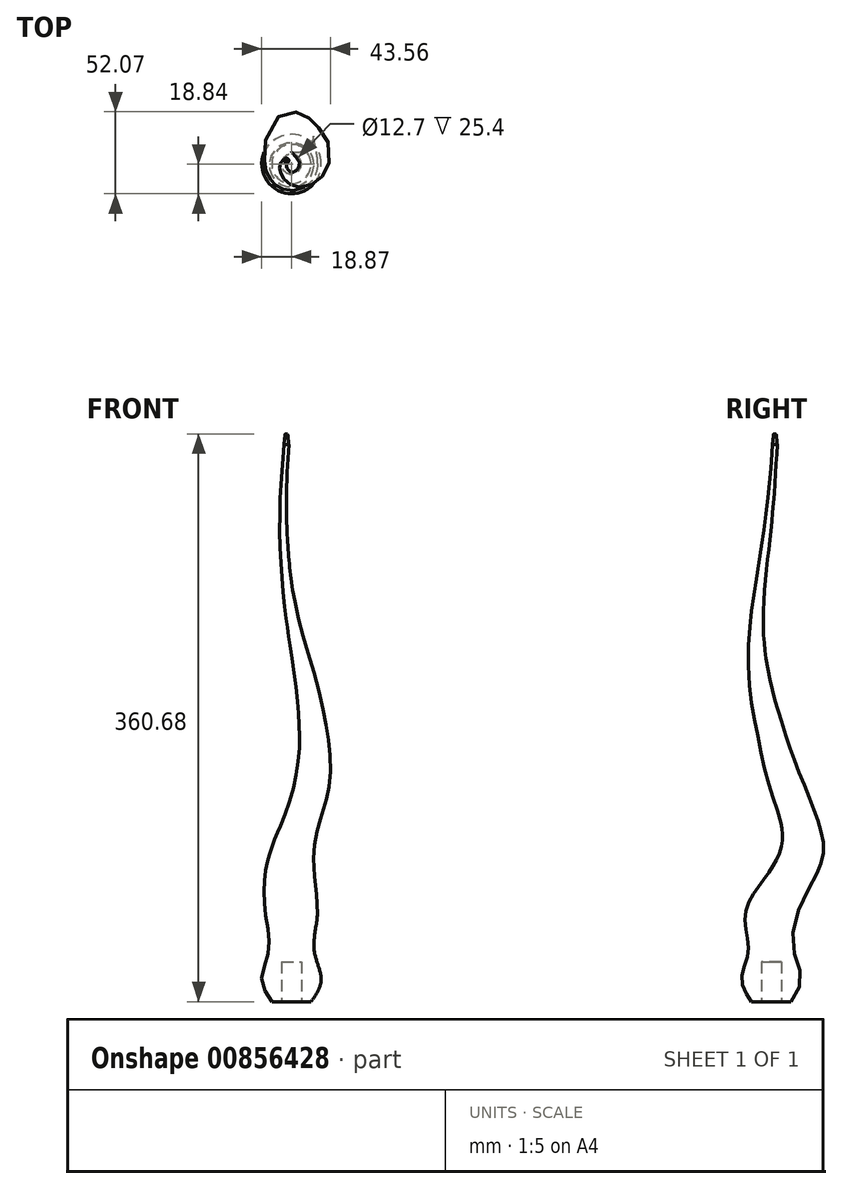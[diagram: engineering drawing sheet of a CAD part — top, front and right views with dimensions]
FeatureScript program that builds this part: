
annotation { "Feature Type Name" : "Feature", "Feature Type Description" : "" }
export const myFeature = defineFeature(function(context is Context, id is Id, definition is map)
    precondition{}
    {
        {
            var Q0;
            Q0=qCreatedBy(makeId("Top.planeOp"),FACE);
            cPlane(context, id + "F0", {"entities" : qUnion([Q0]), "cplaneType" : CPlaneType.OFFSET, "offset" : 38.1 * mm, "width" : 152.4 * mm, "height" : 152.4 * mm});
        }
        {
            var Q0;
            Q0=qCreatedBy(id+"F0.planeOp",FACE);
            cPlane(context, id + "F1", {"entities" : qUnion([Q0]), "cplaneType" : CPlaneType.OFFSET, "offset" : 38.1 * mm, "width" : 152.4 * mm, "height" : 152.4 * mm});
        }
        {
            var Q0;
            Q0=qCreatedBy(id+"F1.planeOp",FACE);
            cPlane(context, id + "F2", {"entities" : qUnion([Q0]), "cplaneType" : CPlaneType.OFFSET, "offset" : 38.1 * mm, "width" : 152.4 * mm, "height" : 152.4 * mm});
        }
        {
            var Q0;
            Q0=qCreatedBy(makeId("Top.planeOp"),FACE);
            var sketch = newSketch(context, id + "F3", { "sketchPlane" : qUnion([Q0])});
            skCircle(sketch, "E0", {"center": v(0, 0) * mm, "radius": 16.51 * mm});
            skSolve(sketch);
        }
        {
            var Q0;
            Q0=qCreatedBy(id+"F0.planeOp",FACE);
            var sketch = newSketch(context, id + "F4", { "sketchPlane" : qUnion([Q0])});
            skCircle(sketch, "E1", {"center": v(0, 19.05) * mm, "radius": 13.97 * mm});
            skLineSegment(sketch, "E2.1", {"start": v(13.47, 13.47) * mm, "end": v(19.05, 0) * mm});
            skLineSegment(sketch, "E2.2", {"start": v(19.05, 0) * mm, "end": v(13.47, -13.47) * mm});
            skLineSegment(sketch, "E2.3", {"start": v(13.47, -13.47) * mm, "end": v(0, -19.05) * mm});
            skLineSegment(sketch, "E2.4", {"start": v(0, -19.05) * mm, "end": v(-13.47, -13.47) * mm});
            skLineSegment(sketch, "E2.5", {"start": v(-13.47, -13.47) * mm, "end": v(-19.05, 0) * mm});
            skLineSegment(sketch, "E2.6", {"start": v(-19.05, 0) * mm, "end": v(-13.47, 13.47) * mm});
            skSolve(sketch);
        }
        {
            var Q0;
            Q0=qCreatedBy(id+"F1.planeOp",FACE);
            var sketch = newSketch(context, id + "F5", { "sketchPlane" : qUnion([Q0])});
            skCircle(sketch, "E3", {"center": v(11.67, 11.67) * mm, "radius": 11.43 * mm});
            skCircle(sketch, "E4.cCircle", {"center": v(0, 0) * mm, "radius": 16.51 * mm, "construction": true});
            skLineSegment(sketch, "E4.2", {"start": v(16.51, 0) * mm, "end": v(11.67, -11.67) * mm});
            skLineSegment(sketch, "E4.3", {"start": v(11.67, -11.67) * mm, "end": v(0, -16.51) * mm});
            skLineSegment(sketch, "E4.4", {"start": v(0, -16.51) * mm, "end": v(-11.67, -11.67) * mm});
            skLineSegment(sketch, "E4.5", {"start": v(-11.67, -11.67) * mm, "end": v(-16.51, 0) * mm});
            skLineSegment(sketch, "E4.6", {"start": v(-16.51, 0) * mm, "end": v(-11.67, 11.67) * mm});
            skLineSegment(sketch, "E4.7", {"start": v(-11.67, 11.67) * mm, "end": v(0, 16.51) * mm});
            skSolve(sketch);
        }
        {
            var Q0;
            Q0=qCreatedBy(id+"F2.planeOp",FACE);
            var sketch = newSketch(context, id + "F6", { "sketchPlane" : qUnion([Q0])});
            skCircle(sketch, "E5.cCircle", {"center": v(0, 0) * mm, "radius": 13.97 * mm, "construction": true});
            skLineSegment(sketch, "E5.0", {"start": v(0, -13.97) * mm, "end": v(-9.88, -9.88) * mm});
            skLineSegment(sketch, "E5.1", {"start": v(-9.88, -9.88) * mm, "end": v(-13.97, 0) * mm});
            skLineSegment(sketch, "E5.2", {"start": v(-13.97, 0) * mm, "end": v(-9.88, 9.88) * mm});
            skLineSegment(sketch, "E5.3", {"start": v(-9.88, 9.88) * mm, "end": v(0, 13.97) * mm});
            skLineSegment(sketch, "E5.4", {"start": v(0, 13.97) * mm, "end": v(9.88, 9.88) * mm});
            skLineSegment(sketch, "E5.7", {"start": v(9.88, -9.88) * mm, "end": v(0, -13.97) * mm});
            skCircle(sketch, "E6", {"center": v(13.97, 0) * mm, "radius": 8.9 * mm});
            skSolve(sketch);
        }
        {
            var Q0;
            Q0=qCreatedBy(id+"F2.planeOp",FACE);
            cPlane(context, id + "F7", {"entities" : qUnion([Q0]), "cplaneType" : CPlaneType.OFFSET, "offset" : 38.1 * mm, "width" : 152.4 * mm, "height" : 152.4 * mm});
        }
        {
            var Q0;
            Q0=qCreatedBy(id+"F7.planeOp",FACE);
            cPlane(context, id + "F8", {"entities" : qUnion([Q0]), "cplaneType" : CPlaneType.OFFSET, "offset" : 38.1 * mm, "width" : 152.4 * mm, "height" : 152.4 * mm});
        }
        {
            var Q0;
            Q0=qCreatedBy(id+"F7.planeOp",FACE);
            var sketch = newSketch(context, id + "F9", { "sketchPlane" : qUnion([Q0])});
            skCircle(sketch, "E7.cCircle", {"center": v(0, 0) * mm, "radius": 11.43 * mm, "construction": true});
            skLineSegment(sketch, "E7.0", {"start": v(0, 11.43) * mm, "end": v(8.08, 8.08) * mm});
            skLineSegment(sketch, "E7.1", {"start": v(8.08, 8.08) * mm, "end": v(11.43, 0) * mm});
            skLineSegment(sketch, "E7.4", {"start": v(0, -11.43) * mm, "end": v(-8.08, -8.08) * mm});
            skLineSegment(sketch, "E7.5", {"start": v(-8.08, -8.08) * mm, "end": v(-11.43, 0) * mm});
            skLineSegment(sketch, "E7.6", {"start": v(-11.43, 0) * mm, "end": v(-8.08, 8.08) * mm});
            skLineSegment(sketch, "E7.7", {"start": v(-8.08, 8.08) * mm, "end": v(0, 11.43) * mm});
            skCircle(sketch, "E8", {"center": v(8.08, -8.08) * mm, "radius": 6.35 * mm});
            skSolve(sketch);
        }
        {
            var Q0;
            Q0=qCreatedBy(id+"F8.planeOp",FACE);
            var sketch = newSketch(context, id + "F10", { "sketchPlane" : qUnion([Q0])});
            skCircle(sketch, "E9.cCircle", {"center": v(0, 0) * mm, "radius": 8.9 * mm, "construction": true});
            skLineSegment(sketch, "E9.0", {"start": v(0, 8.9) * mm, "end": v(6.29, 6.29) * mm});
            skLineSegment(sketch, "E9.1", {"start": v(6.29, 6.29) * mm, "end": v(8.9, 0) * mm});
            skLineSegment(sketch, "E9.2", {"start": v(8.9, 0) * mm, "end": v(6.29, -6.29) * mm});
            skLineSegment(sketch, "E9.5", {"start": v(-6.29, -6.29) * mm, "end": v(-8.9, 0) * mm});
            skLineSegment(sketch, "E9.6", {"start": v(-8.9, 0) * mm, "end": v(-6.29, 6.29) * mm});
            skLineSegment(sketch, "E9.7", {"start": v(-6.29, 6.29) * mm, "end": v(0, 8.9) * mm});
            skCircle(sketch, "E10", {"center": v(0, -8.9) * mm, "radius": 3.8 * mm});
            skSolve(sketch);
        }
        {
            var Q0;
            Q0=qCreatedBy(id+"F8.planeOp",FACE);
            cPlane(context, id + "F11", {"entities" : qUnion([Q0]), "cplaneType" : CPlaneType.OFFSET, "offset" : 38.1 * mm, "width" : 152.4 * mm, "height" : 152.4 * mm});
        }
        {
            var Q0;
            Q0=qCreatedBy(id+"F11.planeOp",FACE);
            cPlane(context, id + "F12", {"entities" : qUnion([Q0]), "cplaneType" : CPlaneType.OFFSET, "offset" : 38.1 * mm, "width" : 152.4 * mm, "height" : 152.4 * mm});
        }
        {
            var Q0;
            Q0=qCreatedBy(id+"F11.planeOp",FACE);
            var sketch = newSketch(context, id + "F13", { "sketchPlane" : qUnion([Q0])});
            skCircle(sketch, "E11.cCircle", {"center": v(0, 0) * mm, "radius": 6.35 * mm, "construction": true});
            skLineSegment(sketch, "E11.0", {"start": v(0, 6.35) * mm, "end": v(4.5, 4.5) * mm});
            skLineSegment(sketch, "E11.1", {"start": v(4.5, 4.5) * mm, "end": v(6.35, 0) * mm});
            skLineSegment(sketch, "E11.2", {"start": v(6.35, 0) * mm, "end": v(4.5, -4.5) * mm});
            skLineSegment(sketch, "E11.3", {"start": v(4.5, -4.5) * mm, "end": v(0, -6.35) * mm});
            skLineSegment(sketch, "E11.6", {"start": v(-6.35, 0) * mm, "end": v(-4.5, 4.5) * mm});
            skLineSegment(sketch, "E11.7", {"start": v(-4.5, 4.5) * mm, "end": v(0, 6.35) * mm});
            skCircle(sketch, "E12", {"center": v(-4.5, -4.5) * mm, "radius": 2.54 * mm});
            skSolve(sketch);
        }
        {
            var Q0;
            Q0=qCreatedBy(id+"F12.planeOp",FACE);
            var sketch = newSketch(context, id + "F14", { "sketchPlane" : qUnion([Q0])});
            skCircle(sketch, "E13.cCircle", {"center": v(0, 0) * mm, "radius": 5.08 * mm, "construction": true});
            skLineSegment(sketch, "E13.1", {"start": v(-3.6, 3.6) * mm, "end": v(0, 5.08) * mm});
            skLineSegment(sketch, "E13.2", {"start": v(0, 5.08) * mm, "end": v(3.6, 3.6) * mm});
            skLineSegment(sketch, "E13.3", {"start": v(3.6, 3.6) * mm, "end": v(5.08, 0) * mm});
            skLineSegment(sketch, "E13.4", {"start": v(5.08, 0) * mm, "end": v(3.6, -3.6) * mm});
            skLineSegment(sketch, "E13.5", {"start": v(3.6, -3.6) * mm, "end": v(0, -5.08) * mm});
            skLineSegment(sketch, "E13.6", {"start": v(0, -5.08) * mm, "end": v(-3.6, -3.6) * mm});
            skCircle(sketch, "E14", {"center": v(-5.08, 0) * mm, "radius": 1.9 * mm});
            skSolve(sketch);
        }
        {
            var Q0;
            Q0=qCreatedBy(id+"F12.planeOp",FACE);
            cPlane(context, id + "F15", {"entities" : qUnion([Q0]), "cplaneType" : CPlaneType.OFFSET, "offset" : 38.1 * mm, "width" : 152.4 * mm, "height" : 152.4 * mm});
        }
        {
            var Q0;
            Q0=qCreatedBy(id+"F15.planeOp",FACE);
            var sketch = newSketch(context, id + "F16", { "sketchPlane" : qUnion([Q0])});
            skCircle(sketch, "E15.cCircle", {"center": v(0, 0) * mm, "radius": 3.81 * mm, "construction": true});
            skLineSegment(sketch, "E15.0", {"start": v(0, 3.81) * mm, "end": v(2.7, 2.7) * mm});
            skLineSegment(sketch, "E15.1", {"start": v(2.7, 2.7) * mm, "end": v(3.8, 0) * mm});
            skLineSegment(sketch, "E15.2", {"start": v(3.81, 0) * mm, "end": v(2.7, -2.7) * mm});
            skLineSegment(sketch, "E15.3", {"start": v(2.7, -2.7) * mm, "end": v(0, -3.8) * mm});
            skLineSegment(sketch, "E15.4", {"start": v(0, -3.8) * mm, "end": v(-2.7, -2.7) * mm});
            skLineSegment(sketch, "E15.5", {"start": v(-2.7, -2.7) * mm, "end": v(-3.8, 0) * mm});
            skCircle(sketch, "E16", {"center": v(-2.7, 2.7) * mm, "radius": 1.52 * mm});
            skSolve(sketch);
        }
        {
            var Q0;
            Q0=qCreatedBy(makeId("Top.planeOp"),FACE);
            cPlane(context, id + "F17", {"entities" : qUnion([Q0]), "cplaneType" : CPlaneType.OFFSET, "offset" : 25.4 * mm, "oppositeDirection" : true, "width" : 152.4 * mm, "height" : 152.4 * mm});
        }
        {
            var Q0;
            Q0=qCreatedBy(id+"F17.planeOp",FACE);
            var sketch = newSketch(context, id + "F18", { "sketchPlane" : qUnion([Q0])});
            skCircle(sketch, "E17", {"center": v(0, 0) * mm, "radius": 14.78 * mm});
            skSolve(sketch);
        }
        {
            var Q0;
            Q0=qCreatedBy(id+"F17.planeOp",FACE);
            cPlane(context, id + "F19", {"entities" : qUnion([Q0]), "cplaneType" : CPlaneType.OFFSET, "offset" : 5.08 * mm, "oppositeDirection" : true, "width" : 152.4 * mm, "height" : 152.4 * mm});
        }
        {
            var Q0;
            Q0=qCreatedBy(id+"F19.planeOp",FACE);
            cPlane(context, id + "F20", {"entities" : qUnion([Q0]), "cplaneType" : CPlaneType.OFFSET, "offset" : 12.7 * mm, "oppositeDirection" : true, "width" : 152.4 * mm, "height" : 152.4 * mm});
        }
        {
            var Q0;
            Q0=qCreatedBy(id+"F20.planeOp",FACE);
            var sketch = newSketch(context, id + "F21", { "sketchPlane" : qUnion([Q0])});
            skCircle(sketch, "E18", {"center": v(0, 0) * mm, "radius": 18.8 * mm});
            skSolve(sketch);
        }
        {
            var Q0;
            Q0=qCreatedBy(id+"F20.planeOp",FACE);
            cPlane(context, id + "F22", {"entities" : qUnion([Q0]), "cplaneType" : CPlaneType.OFFSET, "offset" : 12.7 * mm, "oppositeDirection" : true, "width" : 152.4 * mm, "height" : 152.4 * mm});
        }
        {
            var Q0;
            Q0=qCreatedBy(id+"F22.planeOp",FACE);
            var sketch = newSketch(context, id + "F23", { "sketchPlane" : qUnion([Q0])});
            skCircle(sketch, "E19", {"center": v(0, 0) * mm, "radius": 12.48 * mm});
            skSolve(sketch);
        }
        {
            var Q0;
            Q0=makeQuery(id+"F23.imprint","IMPRINT",FACE,{"disambiguationData":[TD([[makeQuery(id+"F23.imprint","IMPRINT",EDGE,{"derivedFrom":sQuery(id+"F23.wireOp",EDGE,"E19")}),1.0]])]});
            var Q1;
            Q1=makeQuery(id+"F21.imprint","IMPRINT",FACE,{"disambiguationData":[TD([[makeQuery(id+"F21.imprint","IMPRINT",EDGE,{"derivedFrom":sQuery(id+"F21.wireOp",EDGE,"E18")}),1.0]])]});
            var Q2;
            Q2=makeQuery(id+"F18.imprint","IMPRINT",FACE,{"disambiguationData":[TD([[makeQuery(id+"F18.imprint","IMPRINT",EDGE,{"derivedFrom":sQuery(id+"F18.wireOp",EDGE,"E17")}),1.0]])]});
            var Q3;
            Q3=makeQuery(id+"F3.imprint","IMPRINT",FACE,{"disambiguationData":[TD([[makeQuery(id+"F3.imprint","IMPRINT",EDGE,{"derivedFrom":sQuery(id+"F3.wireOp",EDGE,"E0")}),1.0]])]});
            var Q4;
            Q4=makeQuery(id+"F4.imprint","IMPRINT",FACE,{"disambiguationData":[TD([[makeQuery(id+"F4.imprint","IMPRINT",EDGE,{"derivedFrom":sQuery(id+"F4.wireOp",EDGE,"E1")}),1.0]])]});
            var Q5;
            Q5=makeQuery(id+"F5.imprint","IMPRINT",FACE,{"disambiguationData":[TD([[makeQuery(id+"F5.imprint","IMPRINT",EDGE,{"derivedFrom":sQuery(id+"F5.wireOp",EDGE,"E3")}),1.0]])]});
            var Q6;
            Q6=makeQuery(id+"F6.imprint","IMPRINT",FACE,{"disambiguationData":[TD([[makeQuery(id+"F6.imprint","IMPRINT",EDGE,{"derivedFrom":sQuery(id+"F6.wireOp",EDGE,"E6")}),1.0]])]});
            var Q7;
            Q7=makeQuery(id+"F9.imprint","IMPRINT",FACE,{"disambiguationData":[TD([[makeQuery(id+"F9.imprint","IMPRINT",EDGE,{"derivedFrom":sQuery(id+"F9.wireOp",EDGE,"E8")}),1.0]])]});
            var Q8;
            Q8=makeQuery(id+"F10.imprint","IMPRINT",FACE,{"disambiguationData":[TD([[makeQuery(id+"F10.imprint","IMPRINT",EDGE,{"derivedFrom":sQuery(id+"F10.wireOp",EDGE,"E10")}),1.0]])]});
            var Q9;
            Q9=makeQuery(id+"F13.imprint","IMPRINT",FACE,{"disambiguationData":[TD([[makeQuery(id+"F13.imprint","IMPRINT",EDGE,{"derivedFrom":sQuery(id+"F13.wireOp",EDGE,"E12")}),1.0]])]});
            var Q10;
            Q10=makeQuery(id+"F14.imprint","IMPRINT",FACE,{"disambiguationData":[TD([[makeQuery(id+"F14.imprint","IMPRINT",EDGE,{"derivedFrom":sQuery(id+"F14.wireOp",EDGE,"E14")}),1.0]])]});
            var Q11;
            Q11=makeQuery(id+"F16.imprint","IMPRINT",FACE,{"disambiguationData":[TD([[makeQuery(id+"F16.imprint","IMPRINT",EDGE,{"derivedFrom":sQuery(id+"F16.wireOp",EDGE,"E16")}),1.0]])]});
            loft(context, id + "F24", {"sheetProfilesArray" : [{ "sheetProfileEntities" : qUnion([Q0]) }, { "sheetProfileEntities" : qUnion([Q1]) }, { "sheetProfileEntities" : qUnion([Q2]) }, { "sheetProfileEntities" : qUnion([Q3]) }, { "sheetProfileEntities" : qUnion([Q4]) }, { "sheetProfileEntities" : qUnion([Q5]) }, { "sheetProfileEntities" : qUnion([Q6]) }, { "sheetProfileEntities" : qUnion([Q7]) }, { "sheetProfileEntities" : qUnion([Q8]) }, { "sheetProfileEntities" : qUnion([Q9]) }, { "sheetProfileEntities" : qUnion([Q10]) }, { "sheetProfileEntities" : qUnion([Q11]) }]});
        }
        {
            var Q0;
            Q0=makeQuery(id+"F24.opLoft","MID_CAP_EDGE",EDGE,{"disambiguationData":[OSD([sQuery(id+"F16.wireOp",EDGE,"E16")])],"capPos":11.0});
            chamfer(context, id + "F25", {"entities" : qUnion([Q0]), "chamferType" : ChamferType.TWO_OFFSETS, "width1" : 1.27 * mm, "oppositeDirection" : false, "width2" : 6.86 * mm, "tangentPropagation" : true});
        }
        {
            var Q0;
            Q0=makeQuery(id+"F24.opLoft","CAP_FACE",FACE,{"disambiguationData":[OSD([makeQuery(id+"F23.imprint","IMPRINT",FACE,{"disambiguationData":[TD([[makeQuery(id+"F23.imprint","IMPRINT",EDGE,{"derivedFrom":sQuery(id+"F23.wireOp",EDGE,"E19")}),1.0]])]})])],"isStart":true});
            var sketch = newSketch(context, id + "F26", { "sketchPlane" : qUnion([Q0])});
            skCircle(sketch, "E20", {"center": v(0, 0) * mm, "radius": 6.35 * mm});
            skSolve(sketch);
        }
        {
            var Q0;
            Q0 = qSketchRegion(id + "F26", true);
            extrude(context, id + "F27", {"entities" : qUnion([Q0]), "operationType" : NewBodyOperationType.REMOVE, "oppositeDirection" : true, "depth" : 25.4 * mm, "offsetDistance" : 25.4 * mm});
        }
    });
